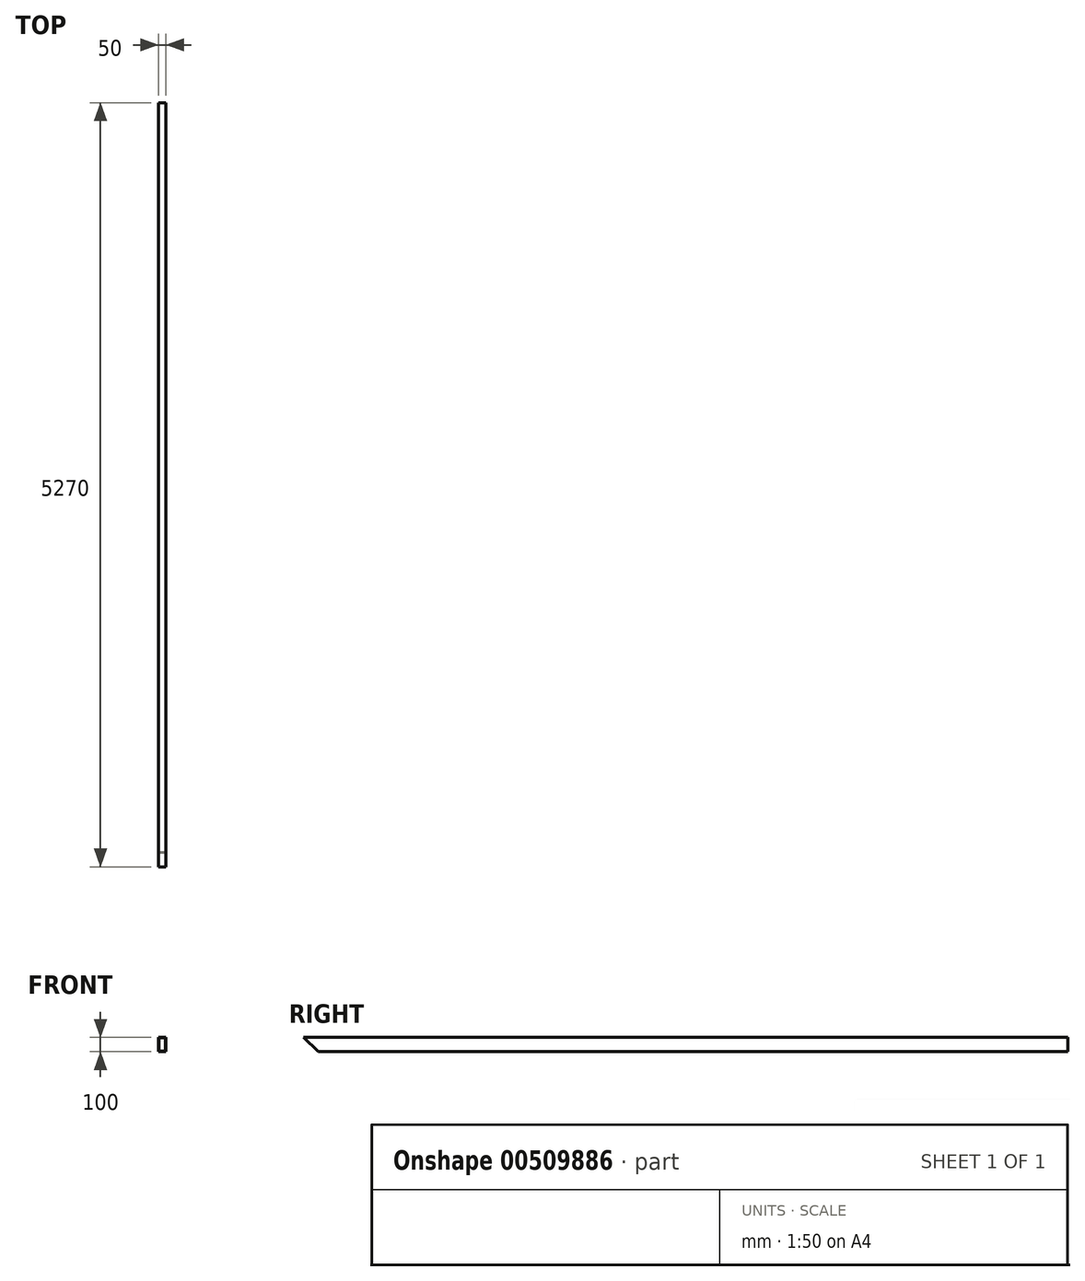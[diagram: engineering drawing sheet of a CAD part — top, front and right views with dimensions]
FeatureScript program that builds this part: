
annotation { "Feature Type Name" : "Feature", "Feature Type Description" : "" }
export const myFeature = defineFeature(function(context is Context, id is Id, definition is map)
    precondition{}
    {
        {
            var Q0;
            Q0=qCreatedBy(makeId("Front.planeOp"),FACE);
            var sketch = newSketch(context, id + "F0", { "sketchPlane" : qUnion([Q0])});
            skLineSegment(sketch, "E0.bottom", {"start": v(15.71, -32) * mm, "end": v(-34.29, -32) * mm});
            skLineSegment(sketch, "E0.top", {"start": v(15.71, 68) * mm, "end": v(-34.29, 68) * mm});
            skLineSegment(sketch, "E0.left", {"start": v(15.71, -32) * mm, "end": v(15.71, 68) * mm});
            skLineSegment(sketch, "E0.right", {"start": v(-34.29, -32) * mm, "end": v(-34.29, 68) * mm});
            skPoint(sketch, "E0.middle", {"position": v(-9.29, 18) * mm});
            skLineSegment(sketch, "E1.bottom", {"start": v(12.71, -29) * mm, "end": v(-31.29, -29) * mm});
            skLineSegment(sketch, "E1.top", {"start": v(12.71, 65) * mm, "end": v(-31.29, 65) * mm});
            skLineSegment(sketch, "E1.left", {"start": v(12.71, -29) * mm, "end": v(12.71, 65) * mm});
            skLineSegment(sketch, "E1.right", {"start": v(-31.29, -29) * mm, "end": v(-31.29, 65) * mm});
            skSolve(sketch);
        }
        {
            var Q0;
            Q0=makeQuery(id+"F0.imprint","IMPRINT",FACE,{"disambiguationData":[TD([[makeQuery(id+"F0.imprint","IMPRINT",EDGE,{"derivedFrom":sQuery(id+"F0.wireOp",EDGE,"E0.bottom")}),-1.0]])]});
            extrude(context, id + "F1", {"entities" : qUnion([Q0]), "depth" : 5270 * mm, "offsetDistance" : 25 * mm});
        }
        {
            var Q0;
            Q0=makeQuery(id+"F1.opExtrude","CAP_EDGE",EDGE,{"disambiguationData":[OSD([sQuery(id+"F0.wireOp",EDGE,"E0.bottom")])],"isStart":false});
            chamfer(context, id + "F2", {"entities" : qUnion([Q0]), "width" : 100 * mm, "tangentPropagation" : true});
        }
    });
